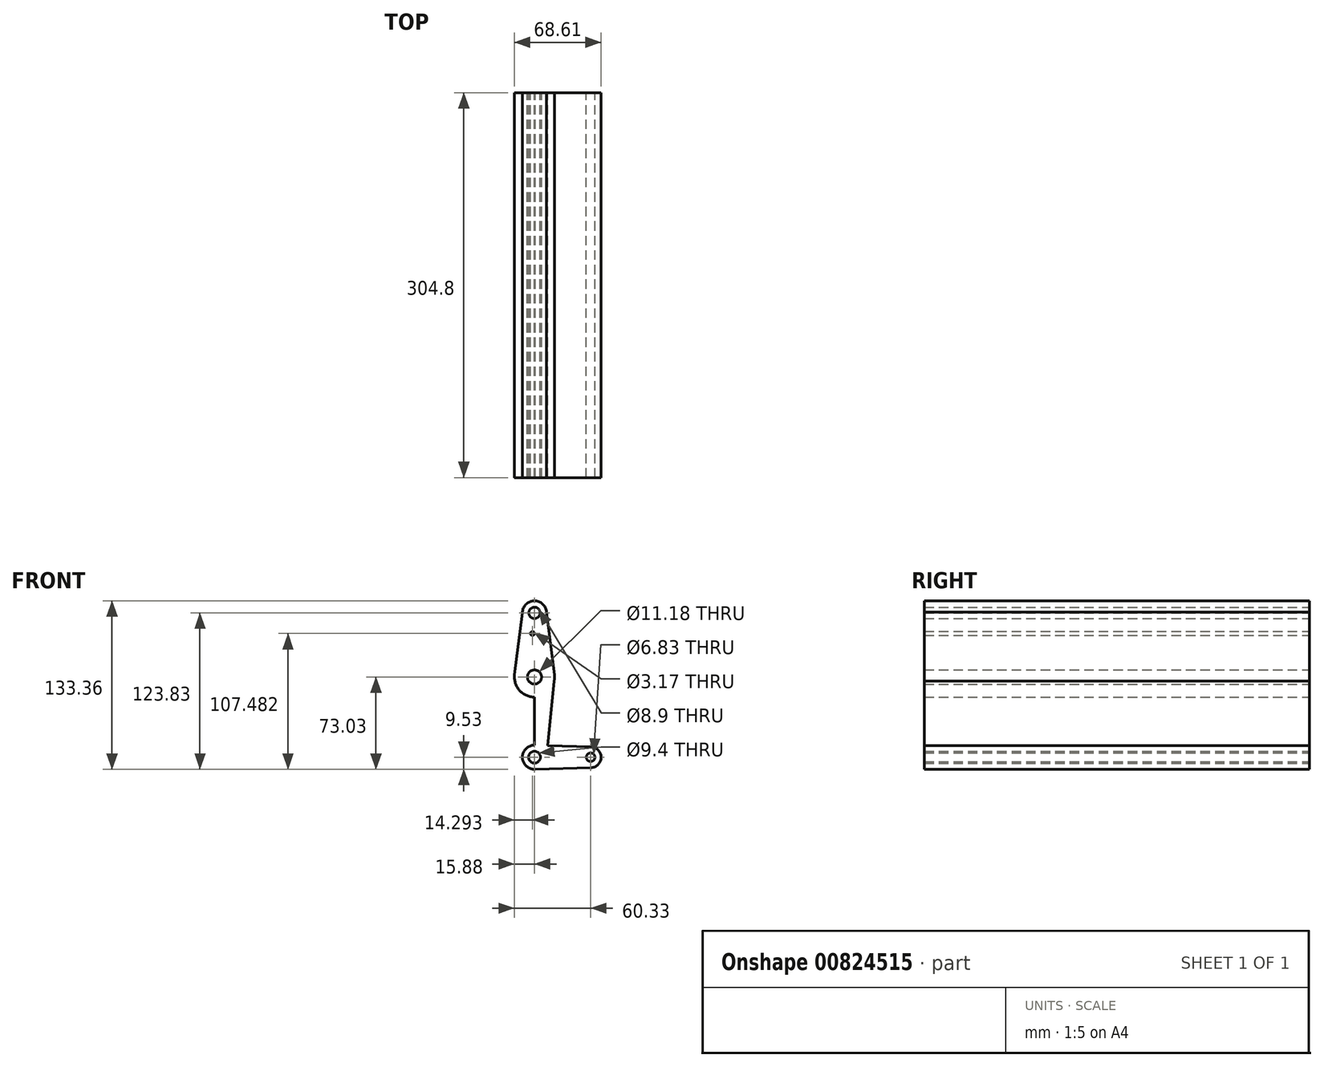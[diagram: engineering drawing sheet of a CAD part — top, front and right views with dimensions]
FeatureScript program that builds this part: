
annotation { "Feature Type Name" : "Feature", "Feature Type Description" : "" }
export const myFeature = defineFeature(function(context is Context, id is Id, definition is map)
    precondition{}
    {
        {
            var Q0;
            Q0=qCreatedBy(makeId("Front.planeOp"),FACE);
            var sketch = newSketch(context, id + "F0", { "sketchPlane" : qUnion([Q0])});
            skLineSegment(sketch, "E0", {"start": v(0, 0) * mm, "end": v(44.45, 0) * mm});
            skCircle(sketch, "E1", {"center": v(0, 114.3) * mm, "radius": 9.52 * mm});
            skCircle(sketch, "E2", {"center": v(44.45, 0) * mm, "radius": 8.28 * mm});
            skCircle(sketch, "E3", {"center": v(0, 0) * mm, "radius": 9.52 * mm});
            skLineSegment(sketch, "E4", {"start": v(0, 114.3) * mm, "end": v(0, 0) * mm});
            skCircle(sketch, "E5", {"center": v(0, 63.5) * mm, "radius": 15.88 * mm});
            skLineSegment(sketch, "E6", {"start": v(0, 63.5) * mm, "end": v(0, 0) * mm});
            skLineSegment(sketch, "E7", {"start": v(9.5, 114.96) * mm, "end": v(15.75, 65.49) * mm});
            skLineSegment(sketch, "E8", {"start": v(-9.52, 114.3) * mm, "end": v(-15.75, 65.5) * mm});
            skCircle(sketch, "E9", {"center": v(-1.59, 97.95) * mm, "radius": 1.59 * mm});
            skCircle(sketch, "E10", {"center": v(0, 63.5) * mm, "radius": 5.59 * mm});
            skCircle(sketch, "E11", {"center": v(0, 114.3) * mm, "radius": 4.45 * mm});
            skCircle(sketch, "E12", {"center": v(0, 0) * mm, "radius": 4.7 * mm});
            skCircle(sketch, "E13", {"center": v(44.45, 0) * mm, "radius": 3.42 * mm});
            skLineSegment(sketch, "E14", {"start": v(0, -9.52) * mm, "end": v(44.68, -8.28) * mm});
            skLineSegment(sketch, "E15", {"start": v(0, 9.52) * mm, "end": v(44.68, 8.28) * mm});
            skLineSegment(sketch, "E16", {"start": v(15.87, 63.64) * mm, "end": v(9.57, 0) * mm});
            skLineSegment(sketch, "E17", {"start": v(-15.87, 63.64) * mm, "end": v(-9.57, 0) * mm});
            skSolve(sketch);
        }
        {
            var Q0;
            Q0 = qSketchRegion(id + "F0", true);
            extrude(context, id + "F1", {"entities" : qUnion([Q0]), "depth" : 304.8 * mm, "offsetDistance" : 25.4 * mm});
        }
    });
